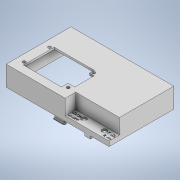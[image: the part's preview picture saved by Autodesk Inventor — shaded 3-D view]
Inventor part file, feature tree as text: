
AUTODESK INVENTOR PART (.ipt)
format: ipt  version: 2020 (Build 240168000, 168)  size: 503,808 bytes
history: native  units: in
note: dims shown in document units (in); Inventor stores cm internally (conversion verified against a paired STEP export)
features: sketch x10, extrude x9, projected_geometry x6, shell x1, plane x1, emboss x1
ambient origin geometry x8: Origin, YZ Plane, XZ Plane, XY Plane, X Axis, Y Axis, Z Axis, Center Point
bodies: Solid1 (feature_tree)
feature tree (28):
  extrude  "Extrusion1"  Depth=3.4in
  extrude  "Extrusion2"  Depth=2.3in
  shell  "Shell1"  Thickness=0.55in
  extrude  "Extrusion3"  Depth=0.1in
  extrude  "Extrusion4"  Depth=0.05in
  extrude  "Extrusion5"  Depth=0.98in
  plane  "Work Plane1"
  extrude  "Extrusion6"  Depth=0.15in TaperAngle=0.0deg
  extrude  "Extrusion7"  Depth=0.01in
  extrude  "Extrusion8"  Depth=0.2in
  extrude  "Extrusion9"  Depth=0.5in TaperAngle=0.0deg
  emboss  "Emboss1"
  sketch  "Sketch1"  dims[d0=5.4in d1=3.4in]
  sketch  "Sketch2"  dims[d2=1.0in d3=0.0in d4=2.3in d5=0.55in]
  sketch  "Sketch3"  dims[d6=0.795in d7=0.0in d8=0.1in]
  projected_geometry  "Projected Loop1"
  sketch  "Sketch4"  dims[d9=0.05in d10=0.05in]
  sketch  "Sketch5"  dims[d11=0.05in d12=0.0in d13=0.98in]
  sketch  "Sketch6"  dims[d14=0.285in d15=0.15in d16=0.05in d17=0.0in d18=0.0in]
  projected_geometry  "Projected Loop2"
  sketch  "Sketch7"  dims[d21=0.1in d22=0.01in]
  projected_geometry  "Projected Loop3"
  projected_geometry  "Projected Loop4"
  sketch  "Sketch8"  dims[d23=0.2405in d25=0.2in]
  projected_geometry  "Projected Loop5"
  projected_geometry  "Projected Loop6"
  sketch  "Sketch9"  dims[d26=0.1in d28=0.5in d29=0.0in]
  sketch  "Sketch10"  dims[d31=0.02in d32=0.075in d33=-1.39in d34=0.01in d35=0.2405in d36=0.11in d38=0.09in d39=0.185in d40=0.033in d41=1.25in d42=0.5in d43=0.0in d44=0.255in d45=0.255in d46=1.075in d47=0.395in d48=0.3475in d49=0.5in d50=0.0in d51=0.15in d52=0.15in d53=1.72in d54=2.74in d55=0.34in d56=0.05in d57=0.05in d58=0.4in d59=0.4in d60=0.05in d61=0.3in d62=0.3in d63=0.5in d64=0.0in d65=0.15in d66=0.15in d67=0.15in d68=0.15in d69=2.32in d70=1.34in d71=0.125in d72=0.1in d73=0.5in d74=0.0in d75=0.2in d76=0.075in d77=0.075in d78=0.05in d79=0.05in d80=0.075in d81=0.0188in d82=0.14in d84=0.125in d85=0.2in d86=0.075in d87=0.05in d88=0.075in d89=0.2in d90=0.075in d91=0.05in d92=0.0188in d93=0.125in d94=0.14in d95=0.01in d96=0.01in d97=0.075in d98=0.0in]
